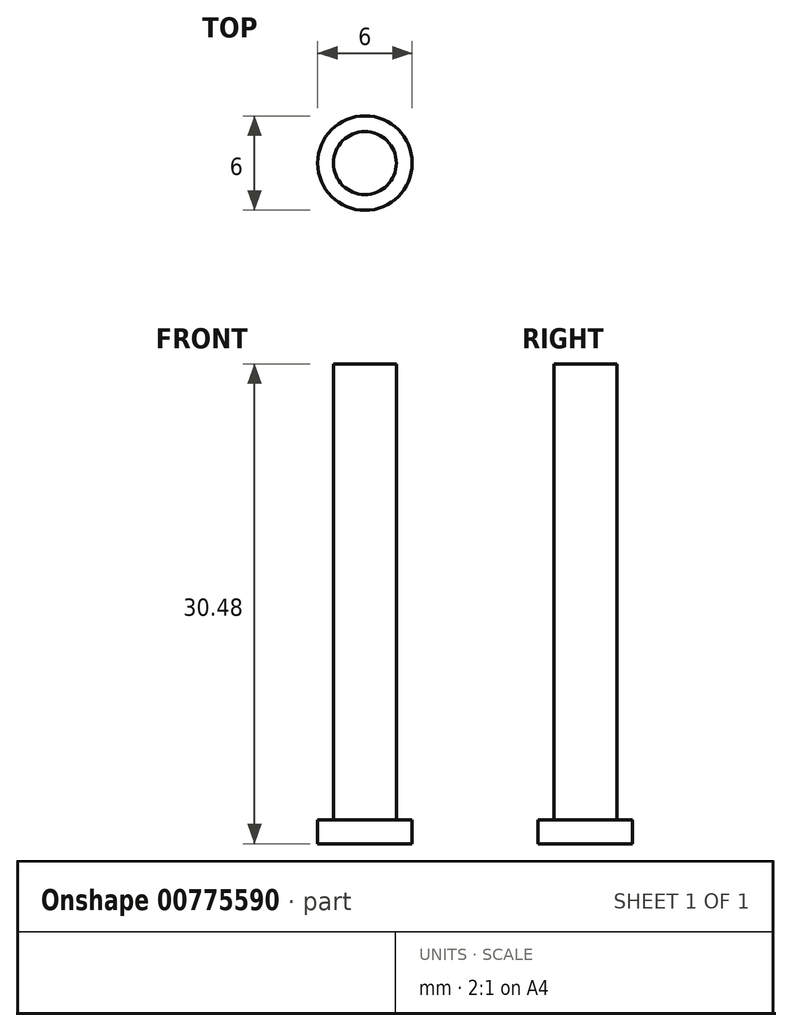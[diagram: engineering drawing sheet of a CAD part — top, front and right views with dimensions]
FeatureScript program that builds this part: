
annotation { "Feature Type Name" : "Feature", "Feature Type Description" : "" }
export const myFeature = defineFeature(function(context is Context, id is Id, definition is map)
    precondition{}
    {
        {
            var Q0;
            Q0=qCreatedBy(makeId("Top.planeOp"),FACE);
            var sketch = newSketch(context, id + "F0", { "sketchPlane" : qUnion([Q0])});
            skCircle(sketch, "E0", {"center": v(0, 0) * mm, "radius": 3 * mm});
            skSolve(sketch);
        }
        {
            var Q0;
            Q0 = qSketchRegion(id + "F0", true);
            extrude(context, id + "F1", {"entities" : qUnion([Q0]), "depth" : 1.5 * mm, "offsetDistance" : 25.4 * mm});
        }
        {
            var Q0;
            Q0=makeQuery(id+"F1.opExtrude","CAP_FACE",FACE,{"disambiguationData":[OSD([sQuery(id+"F0.wireOp",EDGE,"E0")])],"isStart":false});
            var sketch = newSketch(context, id + "F2", { "sketchPlane" : qUnion([Q0])});
            skCircle(sketch, "E1", {"center": v(0, 0) * mm, "radius": 2 * mm});
            skSolve(sketch);
        }
        {
            var Q0;
            Q0 = qSketchRegion(id + "F2", true);
            extrude(context, id + "F3", {"entities" : qUnion([Q0]), "operationType" : NewBodyOperationType.ADD, "depth" : 30.48 * mm - 1.5 * mm, "offsetDistance" : 25.4 * mm});
        }
    });
